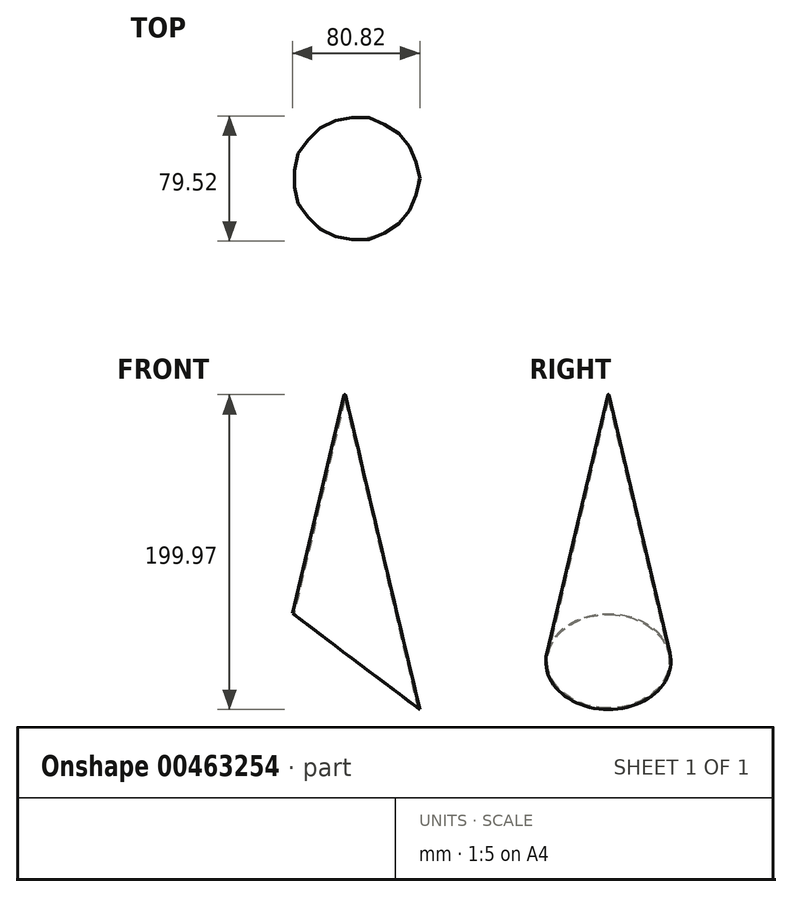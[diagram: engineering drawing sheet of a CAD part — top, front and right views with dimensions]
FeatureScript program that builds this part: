
annotation { "Feature Type Name" : "Feature", "Feature Type Description" : "" }
export const myFeature = defineFeature(function(context is Context, id is Id, definition is map)
    precondition{}
    {
        {
            var Q0;
            Q0=qCreatedBy(makeId("Top.planeOp"),FACE);
            var sketch = newSketch(context, id + "F0", { "sketchPlane" : qUnion([Q0])});
            skCircle(sketch, "E0", {"center": v(0, 0) * mm, "radius": 47.64 * mm});
            skSolve(sketch);
        }
        {
            var Q0;
            Q0=qCreatedBy(makeId("Top.planeOp"),FACE);
            cPlane(context, id + "F1", {"entities" : qUnion([Q0]), "cplaneType" : CPlaneType.OFFSET, "offset" : 200 * mm, "width" : 150 * mm, "height" : 150 * mm});
        }
        {
            var Q0;
            Q0=qCreatedBy(id+"F1.planeOp",FACE);
            var sketch = newSketch(context, id + "F2", { "sketchPlane" : qUnion([Q0])});
            skCircle(sketch, "E1", {"center": v(0, 0) * mm, "radius": 0.32 * mm});
            skSolve(sketch);
        }
        {
            var Q0;
            Q0=makeQuery(id+"F0.imprint","IMPRINT",FACE,{"disambiguationData":[TD([[makeQuery(id+"F0.imprint","IMPRINT",EDGE,{"derivedFrom":sQuery(id+"F0.wireOp",EDGE,"E0")}),1.0]])]});
            var Q1;
            Q1=makeQuery(id+"F2.imprint","IMPRINT",FACE,{"disambiguationData":[TD([[makeQuery(id+"F2.imprint","IMPRINT",EDGE,{"derivedFrom":sQuery(id+"F2.wireOp",EDGE,"E1")}),1.0]])]});
            loft(context, id + "F3", {"sheetProfilesArray" : [{ "sheetProfileEntities" : qUnion([Q0]) }, { "sheetProfileEntities" : qUnion([Q1]) }]});
        }
        {
            var Q0;
            Q0=qCreatedBy(makeId("Front.planeOp"),FACE);
            var sketch = newSketch(context, id + "F4", { "sketchPlane" : qUnion([Q0])});
            skLineSegment(sketch, "E2", {"start": v(47.68, 0) * mm, "end": v(-42.56, 68.16) * mm});
            skLineSegment(sketch, "E3", {"start": v(-42.56, 68.16) * mm, "end": v(-50.64, -6.46) * mm});
            skLineSegment(sketch, "E4", {"start": v(-50.64, -6.46) * mm, "end": v(47.68, 0) * mm});
            skSolve(sketch);
        }
        {
            var Q0;
            Q0=makeQuery(id+"F4.imprint","IMPRINT",FACE,{"disambiguationData":[TD([[makeQuery(id+"F4.imprint","IMPRINT",EDGE,{"derivedFrom":sQuery(id+"F4.wireOp",EDGE,"E2")}),1.0]])]});
            extrude(context, id + "F5", {"entities" : qUnion([Q0]), "operationType" : NewBodyOperationType.REMOVE, "depth" : 107.5 * mm, "hasSecondDirection" : true, "secondDirectionOppositeDirection" : true, "secondDirectionDepth" : 89.4 * mm});
        }
        {
            var Q0;
            Q0=makeQuery(id+"F5.boolean.opBoolean","COPY",FACE,{"derivedFrom":makeQuery(id+"F5.opExtrude","SWEPT_FACE",FACE,{"disambiguationData":[OSD([sQuery(id+"F4.wireOp",EDGE,"E2")])]})});
            shell(context, id + "F6", {"entities" : qUnion([Q0]), "thickness" : 1 * mm});
        }
        {
            var Q0;
            Q0=makeQuery(id+"F3.opLoft","MID_CAP_EDGE",EDGE,{"disambiguationData":[OSD([sQuery(id+"F0.wireOp",EDGE,"E0"),sQuery(id+"F2.wireOp",EDGE,"E1")])],"capPos":1.0});
            fillet(context, id + "F7", {"entities" : qUnion([Q0]), "radius" : 0.18 * mm, "tangentPropagation" : true, "allowEdgeOverflow" : false});
        }
    });
